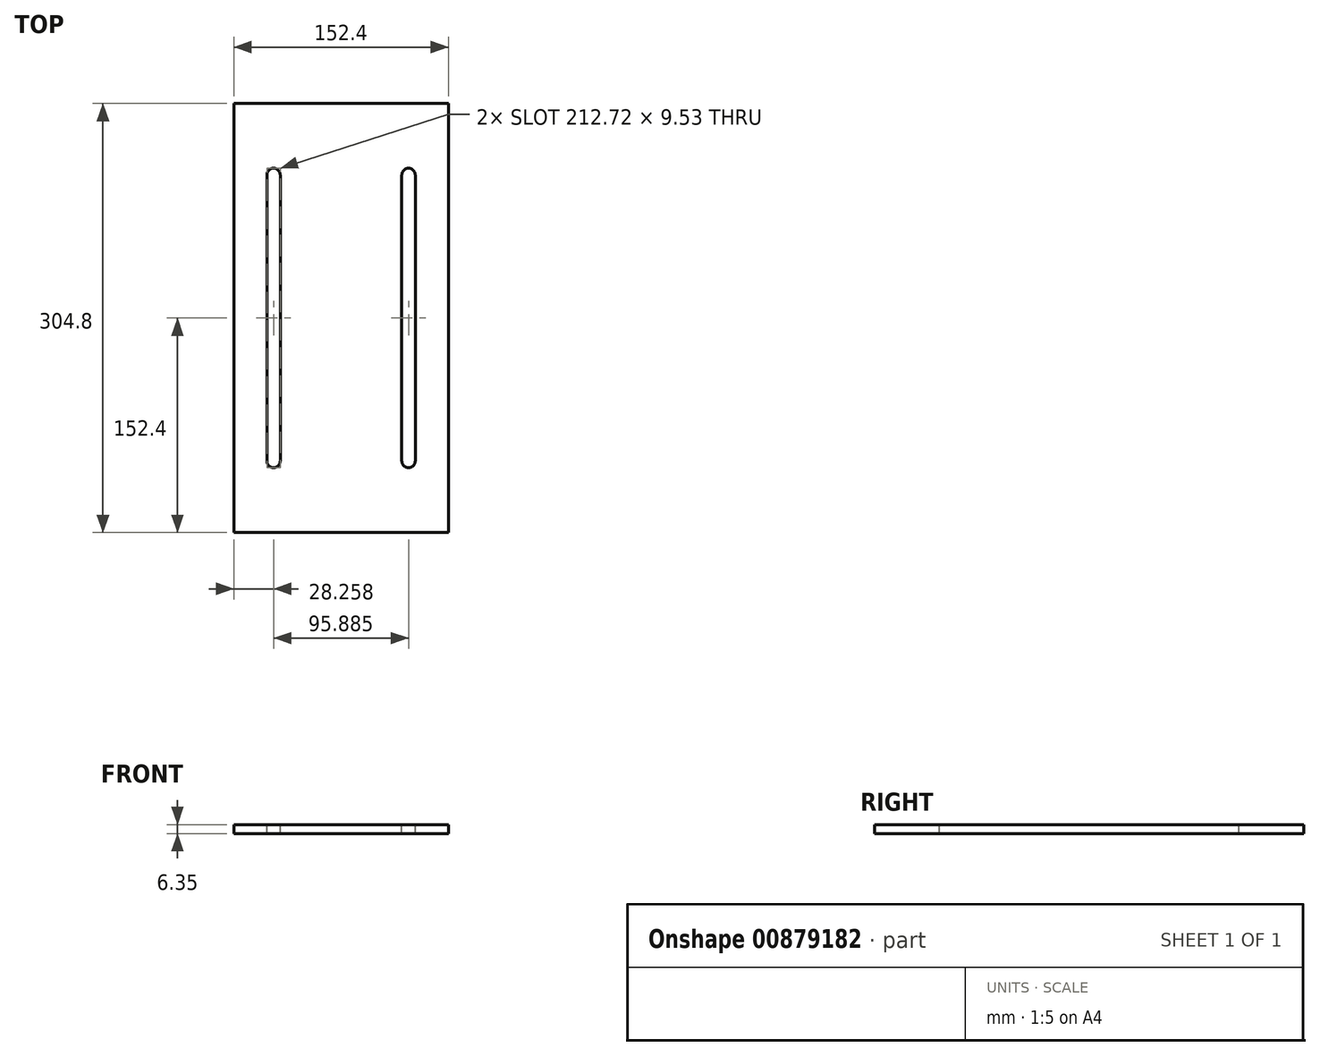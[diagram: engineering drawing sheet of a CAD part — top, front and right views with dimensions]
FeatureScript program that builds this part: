
annotation { "Feature Type Name" : "Feature", "Feature Type Description" : "" }
export const myFeature = defineFeature(function(context is Context, id is Id, definition is map)
    precondition{}
    {
        {
            var Q0;
            Q0=qCreatedBy(makeId("Top.planeOp"),FACE);
            var sketch = newSketch(context, id + "F0", { "sketchPlane" : qUnion([Q0])});
            skLineSegment(sketch, "E0.bottom", {"start": v(0, 0) * mm, "end": v(-152.4, 0) * mm});
            skLineSegment(sketch, "E0.top", {"start": v(0, 304.8) * mm, "end": v(-152.4, 304.8) * mm});
            skLineSegment(sketch, "E0.left", {"start": v(0, 0) * mm, "end": v(0, 304.8) * mm});
            skLineSegment(sketch, "E0.right", {"start": v(-152.4, 0) * mm, "end": v(-152.4, 304.8) * mm});
            skSolve(sketch);
        }
        {
            var Q0;
            Q0=qSketchRegion(id+"F0",true);
            extrude(context, id + "F1", {"entities" : qUnion([Q0]), "depth" : 6.35 * mm, "offsetDistance" : 25.4 * mm});
        }
        {
            var Q0;
            Q0=makeQuery(id+"F1.opExtrude","CAP_FACE",FACE,{"disambiguationData":[OSD([sQuery(id+"F0.wireOp",EDGE,"E0.bottom"),sQuery(id+"F0.wireOp",EDGE,"E0.top"),sQuery(id+"F0.wireOp",EDGE,"E0.left"),sQuery(id+"F0.wireOp",EDGE,"E0.right")])],"isStart":false});
            var sketch = newSketch(context, id + "F2", { "sketchPlane" : qUnion([Q0])});
            skLineSegment(sketch, "E1.bottom", {"start": v(-128.9, 254) * mm, "end": v(-119.38, 254) * mm});
            skLineSegment(sketch, "E1.top", {"start": v(-128.9, 50.8) * mm, "end": v(-119.38, 50.8) * mm});
            skLineSegment(sketch, "E1.left", {"start": v(-128.9, 254) * mm, "end": v(-128.9, 50.8) * mm});
            skLineSegment(sketch, "E1.right", {"start": v(-119.38, 254) * mm, "end": v(-119.38, 50.8) * mm});
            skLineSegment(sketch, "E2.bottom", {"start": v(-33.02, 254) * mm, "end": v(-23.5, 254) * mm});
            skLineSegment(sketch, "E2.top", {"start": v(-33.02, 50.8) * mm, "end": v(-23.5, 50.8) * mm});
            skLineSegment(sketch, "E2.left", {"start": v(-33.02, 254) * mm, "end": v(-33.02, 50.8) * mm});
            skLineSegment(sketch, "E2.right", {"start": v(-23.5, 254) * mm, "end": v(-23.5, 50.8) * mm});
            skArc(sketch, "E3", {"start": v(-119.38, 254) * mm, "mid": v(-124.14, 258.76) * mm, "end": v(-128.9, 254) * mm});
            skArc(sketch, "E4", {"start": v(-23.5, 254) * mm, "mid": v(-28.26, 258.76) * mm, "end": v(-33.02, 254) * mm});
            skPoint(sketch, "E4.midSnap0", {"position": v(-28.26, 254) * mm});
            skPoint(sketch, "E4.midSnap1", {"position": v(-124.14, 258.76) * mm});
            skArc(sketch, "E5", {"start": v(-128.9, 50.8) * mm, "mid": v(-124.14, 46.04) * mm, "end": v(-119.38, 50.8) * mm});
            skArc(sketch, "E6", {"start": v(-33.02, 50.8) * mm, "mid": v(-28.26, 46.04) * mm, "end": v(-23.5, 50.8) * mm});
            skSolve(sketch);
        }
        {
            var Q0;
            Q0=qSketchRegion(id+"F2",true);
            extrude(context, id + "F3", {"entities" : qUnion([Q0]), "operationType" : NewBodyOperationType.REMOVE, "oppositeDirection" : true, "depth" : 25.4 * mm, "offsetDistance" : 25.4 * mm});
        }
    });
